# Revit family: KB d=200_Precast-Console Beam_Spæncom
name_source: partatom
category: Structural Framing
revit_build: Autodesk Revit 2014 (Build: 20130308_1515(x64)
units: mm (PartAtom-declared; Revit-internal decimal feet)

## types (9) — shared parameters
Base width = 500 mm  [stored 1.64042 ft]
Height console = 200 mm  [stored 0.656168 ft]
Manufacturer = Spæncom
Width (bjælkekroppen) = 250 mm  [stored 0.82021 ft]
Width console = 150 mm

## per-type parameters (varying)
| type | Height (bjælkekroppen) | Height element | Model |
| KB38/18 | 180 mm  [stored 0.590551 ft] | 380 mm | KB 38/18 |
| KB42/22 | 220 mm  [stored 0.721785 ft] | 420 mm  [stored 1.37795 ft] | KB 42/22 |
| KB47/27 | 270 mm  [stored 0.885827 ft] | 470 mm  [stored 1.54199 ft] | KB 47/27 |
| KB52/32 | 320 mm  [stored 1.04987 ft] | 520 mm  [stored 1.70604 ft] | KB 52/32 |
| KB57/37 | 370 mm  [stored 1.21391 ft] | 570 mm  [stored 1.87008 ft] | KB 57/37 |
| KB50/30 | 300 mm | 500 mm  [stored 1.64042 ft] | KB 50/30 |
| KB60/40 | 400 mm  [stored 1.31234 ft] | 600 mm | KB 60/40 |
| KB70/50 | 500 mm  [stored 1.64042 ft] | 700 mm  [stored 2.29659 ft] | KB 70/50 |
| KB80/60 | 600 mm | 800 mm  [stored 2.62467 ft] | KB 80/60 |

note: [stored X ft] marks values corroborated as IEEE doubles in the binary element streams (Revit-internal decimal feet)

## geometry (parser evidence)
native form markers: Sweep x6
no freeform markers — native parametric forms only
